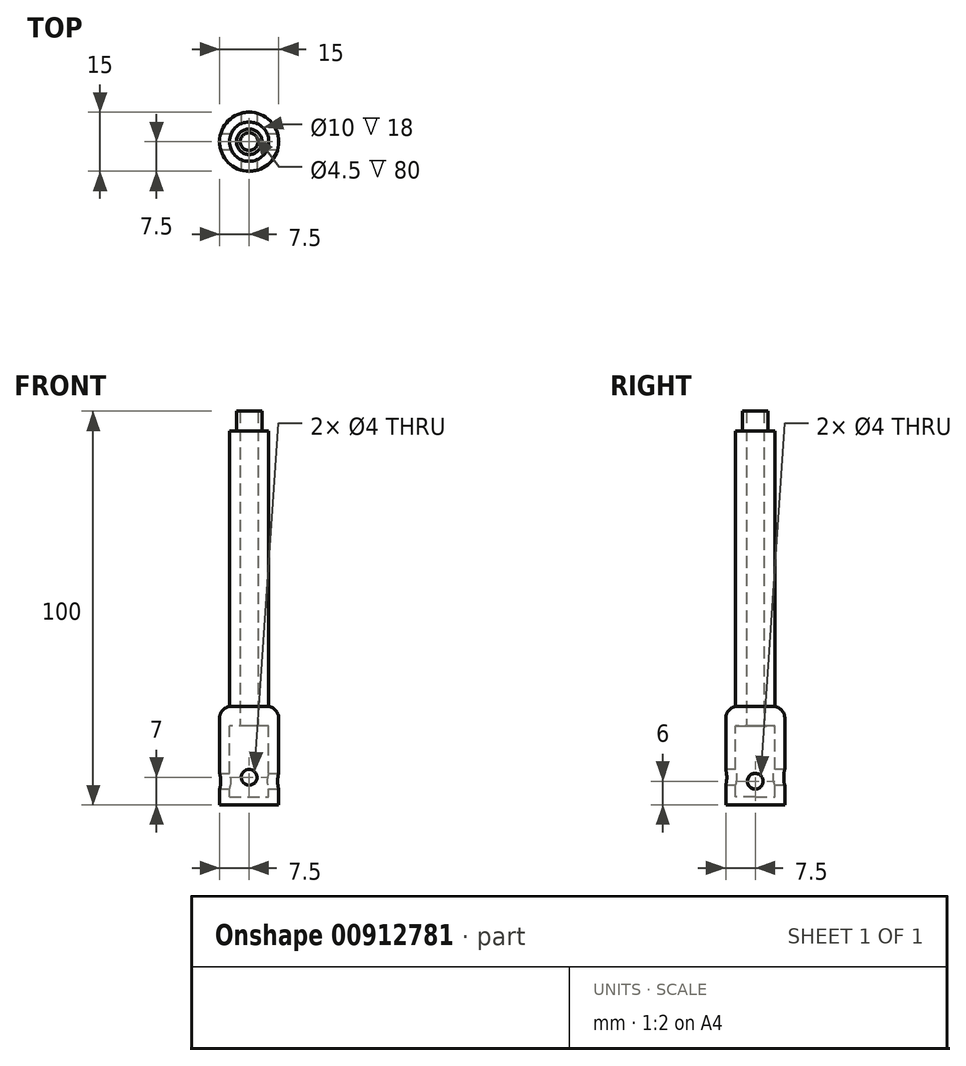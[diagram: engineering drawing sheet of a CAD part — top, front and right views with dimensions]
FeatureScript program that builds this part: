
annotation { "Feature Type Name" : "Feature", "Feature Type Description" : "" }
export const myFeature = defineFeature(function(context is Context, id is Id, definition is map)
    precondition{}
    {
        {
            var Q0;
            Q0=qCreatedBy(makeId("Top.planeOp"),FACE);
            var sketch = newSketch(context, id + "F0", { "sketchPlane" : qUnion([Q0])});
            skCircle(sketch, "E0", {"center": v(0, 0) * mm, "radius": 2.25 * mm});
            skCircle(sketch, "E1", {"center": v(0, 0) * mm, "radius": 3.25 * mm});
            skCircle(sketch, "E2", {"center": v(0, 0) * mm, "radius": 5 * mm});
            skCircle(sketch, "E3", {"center": v(0, 0) * mm, "radius": 7.5 * mm});
            skSolve(sketch);
        }
        {
            var Q0;
            Q0=makeQuery(id+"F0.imprint","IMPRINT",FACE,{"disambiguationData":[TD([[makeQuery(id+"F0.imprint","IMPRINT",EDGE,{"derivedFrom":sQuery(id+"F0.wireOp",EDGE,"E0")}),-1.0]])]});
            extrude(context, id + "F1", {"entities" : qUnion([Q0]), "depth" : 80 * mm, "offsetDistance" : 25 * mm});
        }
        {
            var Q0;
            Q0=makeQuery(id+"F0.imprint","IMPRINT",FACE,{"disambiguationData":[TD([[makeQuery(id+"F0.imprint","IMPRINT",EDGE,{"derivedFrom":sQuery(id+"F0.wireOp",EDGE,"E1")}),-1.0]])]});
            extrude(context, id + "F2", {"entities" : qUnion([Q0]), "operationType" : NewBodyOperationType.ADD, "depth" : 75 * mm, "offsetDistance" : 25 * mm});
        }
        {
            var Q0;
            Q0=makeQuery(id+"F0.imprint","IMPRINT",FACE,{"disambiguationData":[TD([[makeQuery(id+"F0.imprint","IMPRINT",EDGE,{"derivedFrom":sQuery(id+"F0.wireOp",EDGE,"E2")}),-1.0]])]});
            extrude(context, id + "F3", {"entities" : qUnion([Q0]), "operationType" : NewBodyOperationType.ADD, "depth" : 5 * mm, "offsetDistance" : 25 * mm});
        }
        {
            var Q0;
            Q0=makeQuery(id+"F0.imprint","IMPRINT",FACE,{"disambiguationData":[TD([[makeQuery(id+"F0.imprint","IMPRINT",EDGE,{"derivedFrom":sQuery(id+"F0.wireOp",EDGE,"E2")}),-1.0]])]});
            extrude(context, id + "F4", {"entities" : qUnion([Q0]), "operationType" : NewBodyOperationType.ADD, "oppositeDirection" : true, "depth" : 20 * mm, "offsetDistance" : 25 * mm});
        }
        {
            var Q0;
            Q0=makeQuery(id+"F4.opExtrude","CAP_FACE",FACE,{"disambiguationData":[OSD([sQuery(id+"F0.wireOp",EDGE,"E2"),sQuery(id+"F0.wireOp",EDGE,"E3")])],"isStart":false});
            cPlane(context, id + "F5", {"entities" : qUnion([Q0]), "cplaneType" : CPlaneType.OFFSET, "offset" : 0 * mm, "width" : 150 * mm, "height" : 150 * mm});
        }
        {
            var Q0;
            Q0=qCreatedBy(id+"F5.planeOp",FACE);
            var sketch = newSketch(context, id + "F6", { "sketchPlane" : qUnion([Q0])});
            skCircle(sketch, "E4", {"center": v(0, 0) * mm, "radius": 5.5 * mm});
            skSolve(sketch);
        }
        {
            var Q0;
            Q0=qSketchRegion(id+"F6",true);
            extrude(context, id + "F7", {"entities" : qUnion([Q0]), "operationType" : NewBodyOperationType.ADD, "oppositeDirection" : true, "depth" : 2 * mm, "offsetDistance" : 25 * mm});
        }
        {
            var Q0;
            Q0=qCreatedBy(makeId("Front.planeOp"),FACE);
            var sketch = newSketch(context, id + "F8", { "sketchPlane" : qUnion([Q0])});
            skCircle(sketch, "E5", {"center": v(0, -13) * mm, "radius": 2 * mm});
            skSolve(sketch);
        }
        {
            var Q0;
            Q0=qSketchRegion(id+"F8",true);
            extrude(context, id + "F9", {"entities" : qUnion([Q0]), "operationType" : NewBodyOperationType.REMOVE, "endBound" : BoundingType.SYMMETRIC, "oppositeDirection" : true, "depth" : 25 * mm, "offsetDistance" : 25 * mm});
        }
        {
            var Q0;
            Q0=qCreatedBy(makeId("Right.planeOp"),FACE);
            var sketch = newSketch(context, id + "F10", { "sketchPlane" : qUnion([Q0])});
            skCircle(sketch, "E6", {"center": v(0, -14) * mm, "radius": 2 * mm});
            skSolve(sketch);
        }
        {
            var Q0;
            Q0=qSketchRegion(id+"F10",true);
            extrude(context, id + "F11", {"entities" : qUnion([Q0]), "operationType" : NewBodyOperationType.REMOVE, "endBound" : BoundingType.SYMMETRIC, "oppositeDirection" : true, "depth" : 25 * mm, "offsetDistance" : 25 * mm});
        }
        {
            var Q0;
            Q0=makeQuery(id+"F3.opExtrude","CAP_EDGE",EDGE,{"disambiguationData":[OSD([sQuery(id+"F0.wireOp",EDGE,"E3")])],"isStart":false});
            fillet(context, id + "F12", {"entities" : qUnion([Q0]), "radius" : 3 * mm, "tangentPropagation" : true, "allowEdgeOverflow" : false});
        }
    });
